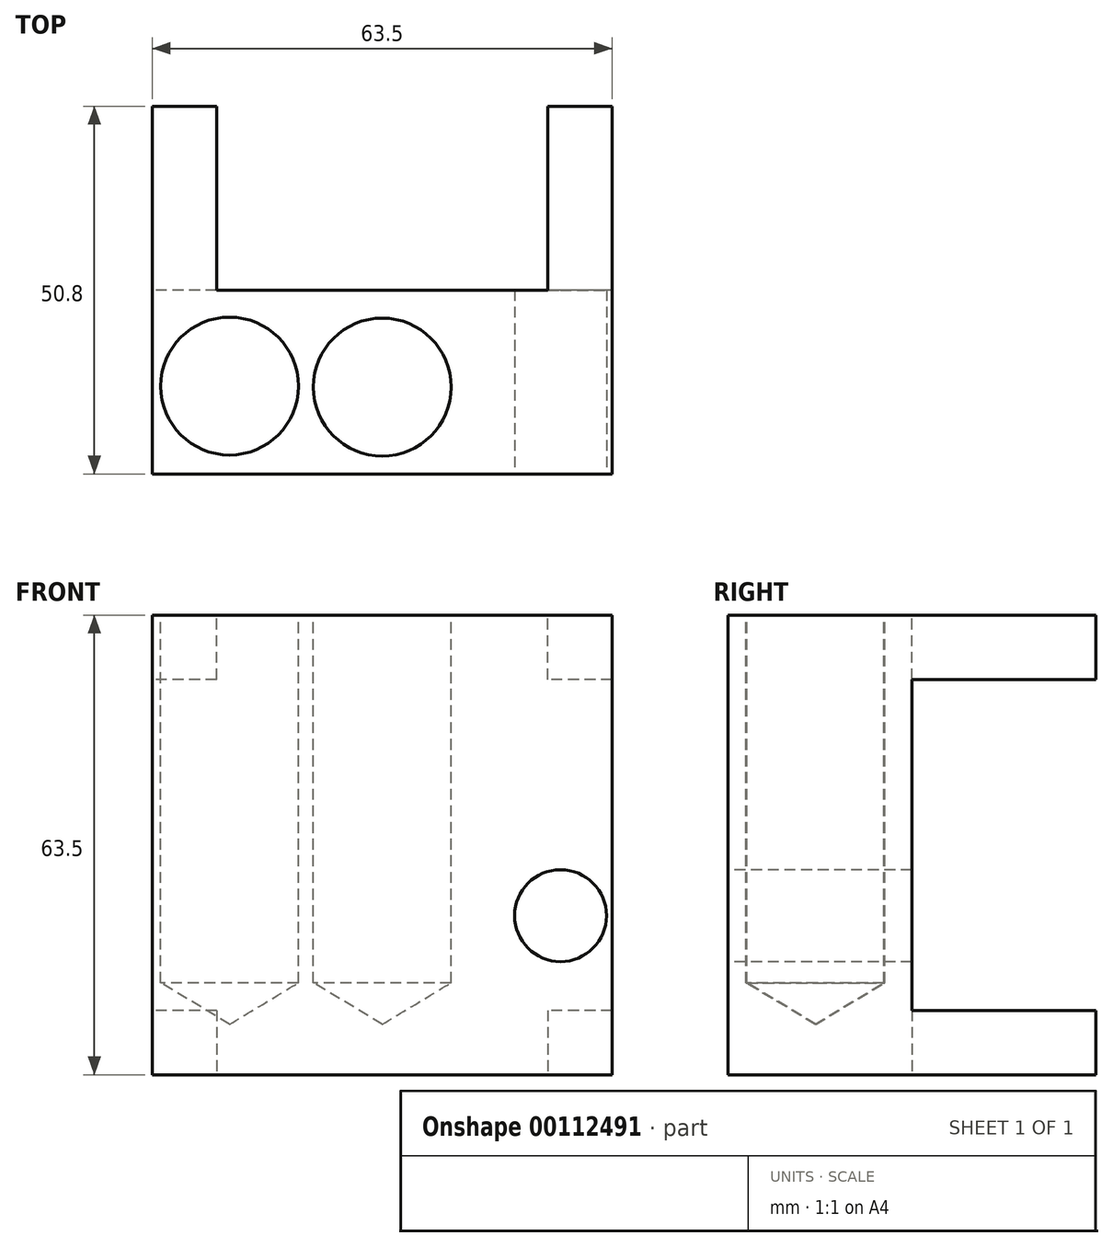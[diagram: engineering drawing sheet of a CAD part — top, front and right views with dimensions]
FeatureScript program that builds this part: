
annotation { "Feature Type Name" : "Feature", "Feature Type Description" : "" }
export const myFeature = defineFeature(function(context is Context, id is Id, definition is map)
    precondition{}
    {
        {
            var Q0;
            Q0=qCreatedBy(makeId("Front.planeOp"),FACE);
            var sketch = newSketch(context, id + "F0", { "sketchPlane" : qUnion([Q0])});
            skLineSegment(sketch, "E0", {"start": v(0, 0) * mm, "end": v(-31.75, 0) * mm});
            skLineSegment(sketch, "E1", {"start": v(0, 0) * mm, "end": v(31.75, 0) * mm});
            skLineSegment(sketch, "E2", {"start": v(-31.75, 0) * mm, "end": v(-31.75, 63.5) * mm});
            skLineSegment(sketch, "E3", {"start": v(-31.75, 63.5) * mm, "end": v(31.75, 63.5) * mm});
            skLineSegment(sketch, "E4", {"start": v(31.75, 63.5) * mm, "end": v(31.75, 0) * mm});
            skLineSegment(sketch, "E5", {"start": v(0, 0) * mm, "end": v(0, 63.5) * mm});
            skSolve(sketch);
        }
        {
            var Q0;
            Q0 = qSketchRegion(id + "F0", true);
            var Q1;
            {var subQ0=sQuery(id+"F0.wireOp",EDGE,"EXIJjChf-3UUV-rYIG-CK25-uzysMGxKMuqJ");var subQ1=sQuery(id+"F0.wireOp",EDGE,"E5");var subQ2=makeQuery(id+"F0.imprint","INTERSECT",VERTEX,{"disambiguationData":[OD(0.0)],"derivedFrom":[subQ1,subQ0]});Q1=makeQuery(id+"F0.imprint","IMPRINT",FACE,{"disambiguationData":[TD([[makeQuery(id+"F0.imprint","IMPRINT",EDGE,{"disambiguationData":[TD([[subQ2,-1.0]])],"derivedFrom":subQ1}),-1.0]])]});}
            var Q2;
            {var subQ0=sQuery(id+"F0.wireOp",EDGE,"EXIJjChf-3UUV-rYIG-CK25-uzysMGxKMuqJ");var subQ1=sQuery(id+"F0.wireOp",EDGE,"E5");var subQ2=makeQuery(id+"F0.imprint","INTERSECT",VERTEX,{"disambiguationData":[OD(0.0)],"derivedFrom":[subQ1,subQ0]});Q2=makeQuery(id+"F0.imprint","IMPRINT",FACE,{"disambiguationData":[TD([[makeQuery(id+"F0.imprint","IMPRINT",EDGE,{"disambiguationData":[TD([[subQ2,-1.0]])],"derivedFrom":subQ1}),1.0]])]});}
            extrude(context, id + "F1", {"entities" : qUnion([Q0, Q1, Q2]), "oppositeDirection" : true, "depth" : 25.4 * mm});
        }
        {
            var Q0;
            {var subQ0=sQuery(id+"F0.wireOp",EDGE,"E3");Q0=makeQuery(id+"Fjn0wVL9m12P33u_1.boolean.opBoolean","MERGE",FACE,{"derivedFrom":[makeQuery(id+"F1.opExtrude","SWEPT_FACE",FACE,{"disambiguationData":[OSD([subQ0])]}),makeQuery(id+"Fjn0wVL9m12P33u_1.opExtrude","SWEPT_FACE",FACE,{"disambiguationData":[OSD([subQ0])]})]});}
            var sketch = newSketch(context, id + "F2", { "sketchPlane" : qUnion([Q0])});
            skLineSegment(sketch, "E6", {"start": v(31.75, 25.4) * mm, "end": v(-31.75, 25.4) * mm});
            skCircle(sketch, "E7", {"center": v(-21.08, 12.13) * mm, "radius": 9.53 * mm});
            skCircle(sketch, "E8", {"center": v(0, 12) * mm, "radius": 9.53 * mm});
            skSolve(sketch);
        }
        {
            var Q0;
            Q0=makeQuery(id+"F1.opExtrude","CAP_FACE",FACE,{"disambiguationData":[OSD([sQuery(id+"F0.wireOp",EDGE,"E0"),sQuery(id+"F0.wireOp",EDGE,"E1"),sQuery(id+"F0.wireOp",EDGE,"E2"),sQuery(id+"F0.wireOp",EDGE,"E3"),sQuery(id+"F0.wireOp",EDGE,"E4")])],"isStart":true});
            var sketch = newSketch(context, id + "F3", { "sketchPlane" : qUnion([Q0])});
            skCircle(sketch, "E9", {"center": v(24.62, 21.97) * mm, "radius": 6.35 * mm});
            skSolve(sketch);
        }
        {
            var Q0;
            Q0=sQuery(id+"F3.wireOp",VERTEX,"E9.center");
            var Q1;
            Q1=makeQuery(id+"F1.opExtrude","SWEPT_BODY",BODY,{"disambiguationData":[OSD([sQuery(id+"F0.wireOp",EDGE,"E0"),sQuery(id+"F0.wireOp",EDGE,"E1"),sQuery(id+"F0.wireOp",EDGE,"E2"),sQuery(id+"F0.wireOp",EDGE,"E3"),sQuery(id+"F0.wireOp",EDGE,"E4")])]});
            hole(context, id + "F4", {"style" : HoleStyle.SIMPLE, "endStyle" : HoleEndStyle.BLIND, "holeDiameter" : 12.7 * mm, "holeDepth" : 25.4 * mm, "locations" : qUnion([Q0]), "scope" : qUnion([Q1])});
        }
        {
            var Q0;
            Q0=makeQuery(id+"F1.opExtrude","CAP_FACE",FACE,{"disambiguationData":[OSD([sQuery(id+"F0.wireOp",EDGE,"E0"),sQuery(id+"F0.wireOp",EDGE,"E1"),sQuery(id+"F0.wireOp",EDGE,"E2"),sQuery(id+"F0.wireOp",EDGE,"E3"),sQuery(id+"F0.wireOp",EDGE,"E4")])],"isStart":false});
            var sketch = newSketch(context, id + "F5", { "sketchPlane" : qUnion([Q0])});
            skLineSegment(sketch, "E10", {"start": v(-31.75, 54.6) * mm, "end": v(31.75, 54.6) * mm});
            skLineSegment(sketch, "E11", {"start": v(-22.86, 54.6) * mm, "end": v(-22.86, 63.5) * mm});
            skLineSegment(sketch, "E12", {"start": v(22.86, 54.6) * mm, "end": v(22.86, 63.5) * mm});
            skLineSegment(sketch, "E13", {"start": v(-31.75, 8.9) * mm, "end": v(31.75, 8.9) * mm});
            skLineSegment(sketch, "E14", {"start": v(22.86, 8.9) * mm, "end": v(22.86, 0) * mm});
            skLineSegment(sketch, "E15", {"start": v(-22.86, 8.9) * mm, "end": v(-22.86, 0) * mm});
            skSolve(sketch);
        }
        {
            var Q0;
            {var subQ3=sQuery(id+"F5.wireOp",EDGE,"E11");Q0=makeQuery(id+"F5.imprint","IMPRINT",FACE,{"disambiguationData":[TD([[makeQuery(id+"F5.imprint","IMPRINT",EDGE,{"derivedFrom":subQ3}),1.0]])]});}
            var Q1;
            {var subQ3=sQuery(id+"F5.wireOp",EDGE,"E12");Q1=makeQuery(id+"F5.imprint","IMPRINT",FACE,{"disambiguationData":[TD([[makeQuery(id+"F5.imprint","IMPRINT",EDGE,{"derivedFrom":subQ3}),-1.0]])]});}
            var Q2;
            {var subQ3=sQuery(id+"F5.wireOp",EDGE,"E15");Q2=makeQuery(id+"F5.imprint","IMPRINT",FACE,{"disambiguationData":[TD([[makeQuery(id+"F5.imprint","IMPRINT",EDGE,{"derivedFrom":subQ3}),-1.0]])]});}
            var Q3;
            {var subQ3=sQuery(id+"F5.wireOp",EDGE,"E14");Q3=makeQuery(id+"F5.imprint","IMPRINT",FACE,{"disambiguationData":[TD([[makeQuery(id+"F5.imprint","IMPRINT",EDGE,{"derivedFrom":subQ3}),1.0]])]});}
            extrude(context, id + "F6", {"entities" : qUnion([Q0, Q1, Q2, Q3]), "operationType" : NewBodyOperationType.ADD, "depth" : 25.4 * mm});
        }
        {
            var Q0;
            Q0=sQuery(id+"F2.wireOp",VERTEX,"E7.center");
            var Q1;
            Q1=sQuery(id+"F2.wireOp",VERTEX,"E8.center");
            var Q2;
            Q2=makeQuery(id+"F1.opExtrude","SWEPT_BODY",BODY,{"disambiguationData":[OSD([sQuery(id+"F0.wireOp",EDGE,"E0"),sQuery(id+"F0.wireOp",EDGE,"E1"),sQuery(id+"F0.wireOp",EDGE,"E2"),sQuery(id+"F0.wireOp",EDGE,"E3"),sQuery(id+"F0.wireOp",EDGE,"E4")])]});
            hole(context, id + "F7", {"style" : HoleStyle.SIMPLE, "endStyle" : HoleEndStyle.BLIND, "holeDiameter" : 19.05 * mm, "holeDepth" : 50.8 * mm, "locations" : qUnion([Q0, Q1]), "scope" : qUnion([Q2])});
        }
    });
